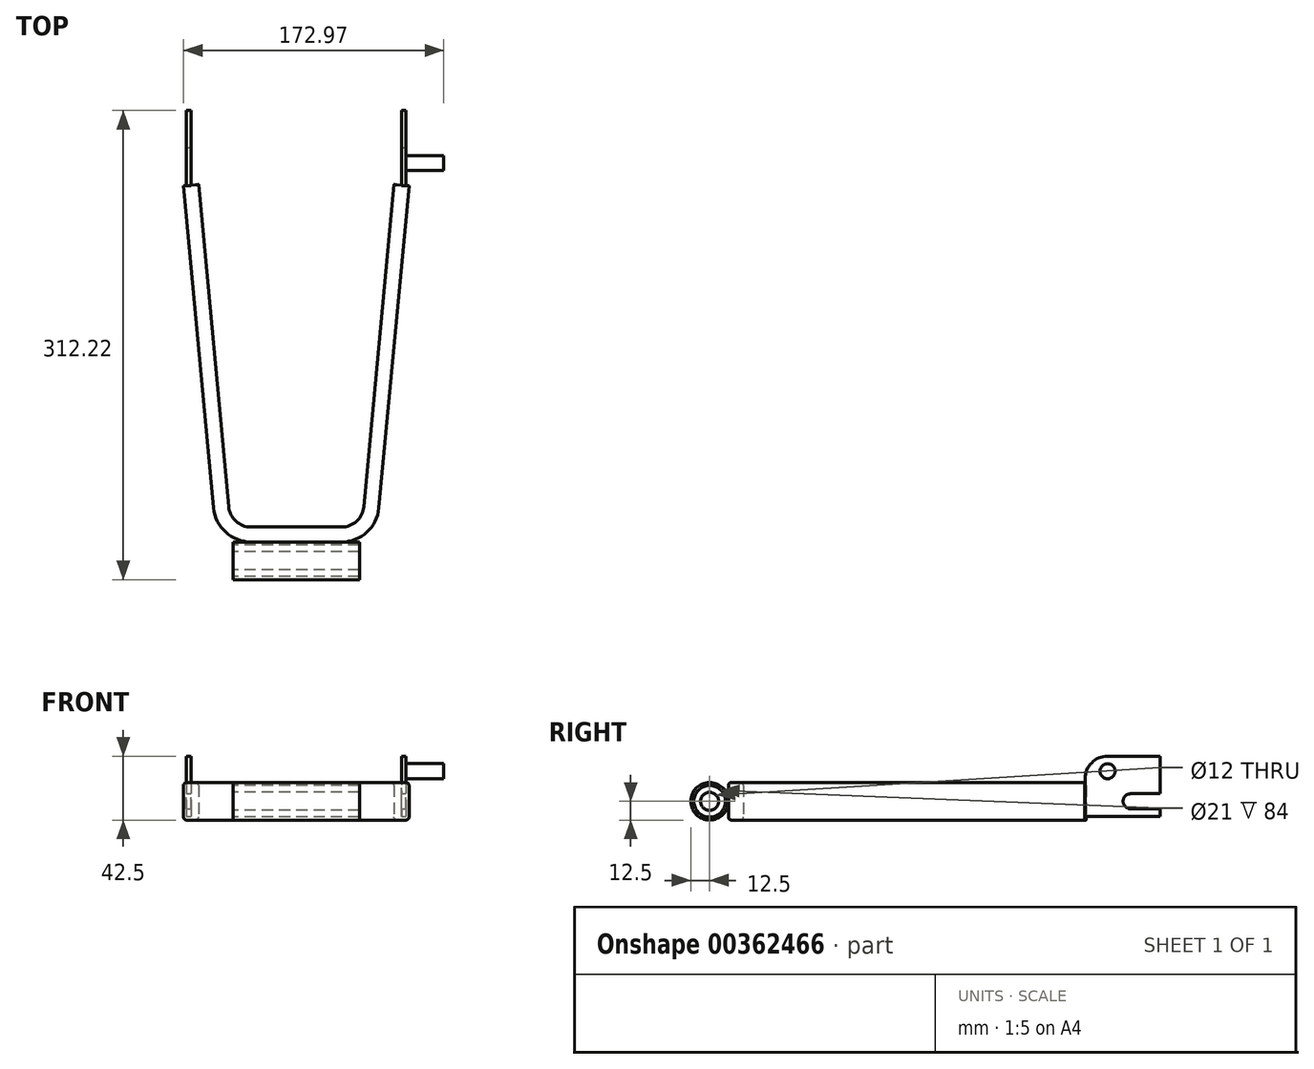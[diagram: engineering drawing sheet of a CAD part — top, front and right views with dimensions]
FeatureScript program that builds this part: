
annotation { "Feature Type Name" : "Feature", "Feature Type Description" : "" }
export const myFeature = defineFeature(function(context is Context, id is Id, definition is map)
    precondition{}
    {
        {
            var Q0;
            Q0=qCreatedBy(makeId("Right.planeOp"),FACE);
            var sketch = newSketch(context, id + "F0", { "sketchPlane" : qUnion([Q0])});
            skCircle(sketch, "E0", {"center": v(0, 0) * mm, "radius": 12.5 * mm});
            skCircle(sketch, "E1", {"center": v(0, 0) * mm, "radius": 10.5 * mm});
            skSolve(sketch);
        }
        {
            var Q0;
            Q0 = qSketchRegion(id + "F0", true);
            extrude(context, id + "F1", {"entities" : qUnion([Q0]), "depth" : 84 * mm, "offsetDistance" : 25 * mm});
        }
        {
            var Q0;
            Q0=qCreatedBy(makeId("Right.planeOp"),FACE);
            var sketch = newSketch(context, id + "F2", { "sketchPlane" : qUnion([Q0])});
            skCircle(sketch, "E2", {"center": v(0, 0) * mm, "radius": 10.5 * mm});
            skCircle(sketch, "E3", {"center": v(0, 0) * mm, "radius": 6 * mm});
            skSolve(sketch);
        }
        {
            var Q0;
            Q0 = qSketchRegion(id + "F2", true);
            extrude(context, id + "F3", {"entities" : qUnion([Q0]), "depth" : 84 * mm, "offsetDistance" : 25 * mm});
        }
        {
            var Q0;
            Q0=qCreatedBy(makeId("Top.planeOp"),FACE);
            var sketch = newSketch(context, id + "F4", { "sketchPlane" : qUnion([Q0])});
            skLineSegment(sketch, "E4", {"start": v(-28, 250) * mm, "end": v(-8, 35.64) * mm});
            skLineSegment(sketch, "E5", {"start": v(11.91, 17.5) * mm, "end": v(72.09, 17.5) * mm});
            skLineSegment(sketch, "E6", {"start": v(92, 35.64) * mm, "end": v(112, 250) * mm});
            skPoint(sketch, "E7.visualSharp", {"position": v(-6.3, 17.5) * mm});
            skArc(sketch, "E7.filletArc", {"start": v(-8, 35.64) * mm, "mid": v(-1.56, 22.72) * mm, "end": v(11.91, 17.5) * mm});
            skPoint(sketch, "E8.visualSharp", {"position": v(90.3, 17.5) * mm});
            skArc(sketch, "E8.filletArc", {"start": v(72.09, 17.5) * mm, "mid": v(85.56, 22.72) * mm, "end": v(92, 35.64) * mm});
            skLineSegment(sketch, "E9", {"start": v(42, 17.5) * mm, "end": v(42, 0) * mm, "construction": true});
            skSolve(sketch);
        }
        {
            var Q0;
            Q0=sQuery(id+"F4.wireOp",VERTEX,"E4.start");
            var Q1;
            Q1=sQuery(id+"F4.wireOp",EDGE,"E4");
            cPlane(context, id + "F5", {"entities" : qUnion([Q0, Q1]), "cplaneType" : CPlaneType.LINE_POINT, "offset" : 25 * mm, "width" : 150 * mm, "height" : 150 * mm});
        }
        {
            var Q0;
            Q0=qCreatedBy(id+"F5.planeOp",FACE);
            var sketch = newSketch(context, id + "F6", { "sketchPlane" : qUnion([Q0])});
            skLineSegment(sketch, "E10.bottom", {"start": v(-7.65, 12.5) * mm, "end": v(-1.65, 12.5) * mm});
            skLineSegment(sketch, "E10.top", {"start": v(-7.65, -12.5) * mm, "end": v(-1.65, -12.5) * mm});
            skLineSegment(sketch, "E10.left", {"start": v(-9.65, 10.5) * mm, "end": v(-9.65, -10.5) * mm});
            skLineSegment(sketch, "E10.right", {"start": v(0.35, 10.5) * mm, "end": v(0.35, -10.5) * mm});
            skPoint(sketch, "E10.middle", {"position": v(-4.65, 0) * mm});
            skPoint(sketch, "E11.visualSharp", {"position": v(-9.65, -12.5) * mm});
            skArc(sketch, "E11.filletArc", {"start": v(-9.65, -10.5) * mm, "mid": v(-9.07, -11.91) * mm, "end": v(-7.65, -12.5) * mm});
            skPoint(sketch, "E12.visualSharp", {"position": v(0.35, -12.5) * mm});
            skArc(sketch, "E12.filletArc", {"start": v(-1.65, -12.5) * mm, "mid": v(-0.24, -11.91) * mm, "end": v(0.35, -10.5) * mm});
            skPoint(sketch, "E13.visualSharp", {"position": v(0.35, 12.5) * mm});
            skArc(sketch, "E13.filletArc", {"start": v(0.35, 10.5) * mm, "mid": v(-0.24, 11.91) * mm, "end": v(-1.65, 12.5) * mm});
            skPoint(sketch, "E14.visualSharp", {"position": v(-9.65, 12.5) * mm});
            skArc(sketch, "E14.filletArc", {"start": v(-7.65, 12.5) * mm, "mid": v(-9.07, 11.91) * mm, "end": v(-9.65, 10.5) * mm});
            skSolve(sketch);
        }
        {
            var Q0;
            Q0 = qSketchRegion(id + "F6", true);
            var Q1;
            Q1 = qConstructionFilter(qBodyType(qCreatedBy(id + "F4" ,EDGE), BodyType.WIRE), ConstructionObject.NO);
            sweep(context, id + "F7", {"profiles" : qUnion([Q0]), "path" : qUnion([Q1])});
        }
        {
            var Q0;
            Q0=qCreatedBy(makeId("Top.planeOp"),FACE);
            var sketch = newSketch(context, id + "F8", { "sketchPlane" : qUnion([Q0])});
            skLineSegment(sketch, "E15", {"start": v(42, 0) * mm, "end": v(42, 179.75) * mm, "construction": true});
            skLineSegment(sketch, "E16.bottom", {"start": v(-30.99, 249.72) * mm, "end": v(-28, 249.72) * mm});
            skLineSegment(sketch, "E16.top", {"start": v(-30.99, 299.72) * mm, "end": v(-28, 299.72) * mm});
            skLineSegment(sketch, "E16.left", {"start": v(-30.99, 249.72) * mm, "end": v(-30.99, 299.72) * mm});
            skLineSegment(sketch, "E16.right", {"start": v(-28, 249.72) * mm, "end": v(-28, 299.72) * mm});
            skLineSegment(sketch, "E17.MirrorCS", {"start": v(114.99, 249.72) * mm, "end": v(112, 249.72) * mm});
            skLineSegment(sketch, "E18.MirrorCS", {"start": v(114.99, 299.72) * mm, "end": v(112, 299.72) * mm});
            skLineSegment(sketch, "E19.MirrorCS", {"start": v(114.99, 249.72) * mm, "end": v(114.99, 299.72) * mm});
            skLineSegment(sketch, "E20.MirrorCS", {"start": v(112, 249.72) * mm, "end": v(112, 299.72) * mm});
            skSolve(sketch);
        }
        {
            var Q0;
            Q0 = qSketchRegion(id + "F8", true);
            extrude(context, id + "F9", {"entities" : qUnion([Q0]), "operationType" : NewBodyOperationType.ADD, "depth" : 30 * mm, "offsetDistance" : 25 * mm, "hasSecondDirection" : true, "secondDirectionOppositeDirection" : true, "secondDirectionDepth" : 10 * mm});
        }
        {
            var Q0;
            Q0=qCreatedBy(makeId("Right.planeOp"),FACE);
            var sketch = newSketch(context, id + "F10", { "sketchPlane" : qUnion([Q0])});
            skArc(sketch, "E21", {"start": v(280, 5) * mm, "mid": v(275, 0) * mm, "end": v(280, -5) * mm});
            skLineSegment(sketch, "E22", {"start": v(280, 5) * mm, "end": v(299.71, 5) * mm});
            skLineSegment(sketch, "E23", {"start": v(299.71, 5) * mm, "end": v(299.71, -5) * mm});
            skLineSegment(sketch, "E24", {"start": v(299.71, -5) * mm, "end": v(280, -5) * mm});
            skSolve(sketch);
        }
        {
            var Q0;
            Q0 = qSketchRegion(id + "F10", true);
            extrude(context, id + "F11", {"entities" : qUnion([Q0]), "operationType" : NewBodyOperationType.REMOVE, "endBound" : BoundingType.THROUGH_ALL, "oppositeDirection" : true, "depth" : 25 * mm, "offsetDistance" : 25 * mm, "hasSecondDirection" : true, "secondDirectionBound" : SecondDirectionBoundingType.THROUGH_ALL, "secondDirectionOppositeDirection" : false, "secondDirectionDepth" : 25 * mm});
        }
        {
            var Q0;
            Q0=makeQuery(id+"F9.opExtrude","CAP_EDGE",EDGE,{"disambiguationData":[OSD([sQuery(id+"F8.wireOp",EDGE,"E17.MirrorCS")])],"isStart":false});
            var Q1;
            Q1=makeQuery(id+"F9.opExtrude","CAP_EDGE",EDGE,{"disambiguationData":[OSD([sQuery(id+"F8.wireOp",EDGE,"E16.bottom")])],"isStart":false});
            fillet(context, id + "F12", {"entities" : qUnion([Q0, Q1]), "radius" : 15 * mm, "tangentPropagation" : true, "allowEdgeOverflow" : false});
        }
        {
            var Q0;
            Q0=makeQuery(id+"F9.opExtrude","SWEPT_FACE",FACE,{"disambiguationData":[OSD([sQuery(id+"F8.wireOp",EDGE,"E19.MirrorCS")])]});
            var sketch = newSketch(context, id + "F13", { "sketchPlane" : qUnion([Q0])});
            skCircle(sketch, "E25", {"center": v(264.72, 20) * mm, "radius": 5 * mm});
            skSolve(sketch);
        }
        {
            var Q0;
            Q0 = qSketchRegion(id + "F13", true);
            extrude(context, id + "F14", {"entities" : qUnion([Q0]), "operationType" : NewBodyOperationType.ADD, "depth" : 25 * mm, "offsetDistance" : 25 * mm});
        }
        {
            var Q0;
            Q0=makeQuery(id+"F9.opExtrude","SWEPT_FACE",FACE,{"disambiguationData":[OSD([sQuery(id+"F8.wireOp",EDGE,"E16.right")])]});
            var Q1;
            Q1=makeQuery(id+"F9.opExtrude","SWEPT_FACE",FACE,{"disambiguationData":[OSD([sQuery(id+"F8.wireOp",EDGE,"E20.MirrorCS")])]});
            cPlane(context, id + "F15", {"entities" : qUnion([Q0, Q1]), "cplaneType" : CPlaneType.MID_PLANE, "offset" : 25 * mm, "width" : 150 * mm, "height" : 150 * mm});
        }
    });
